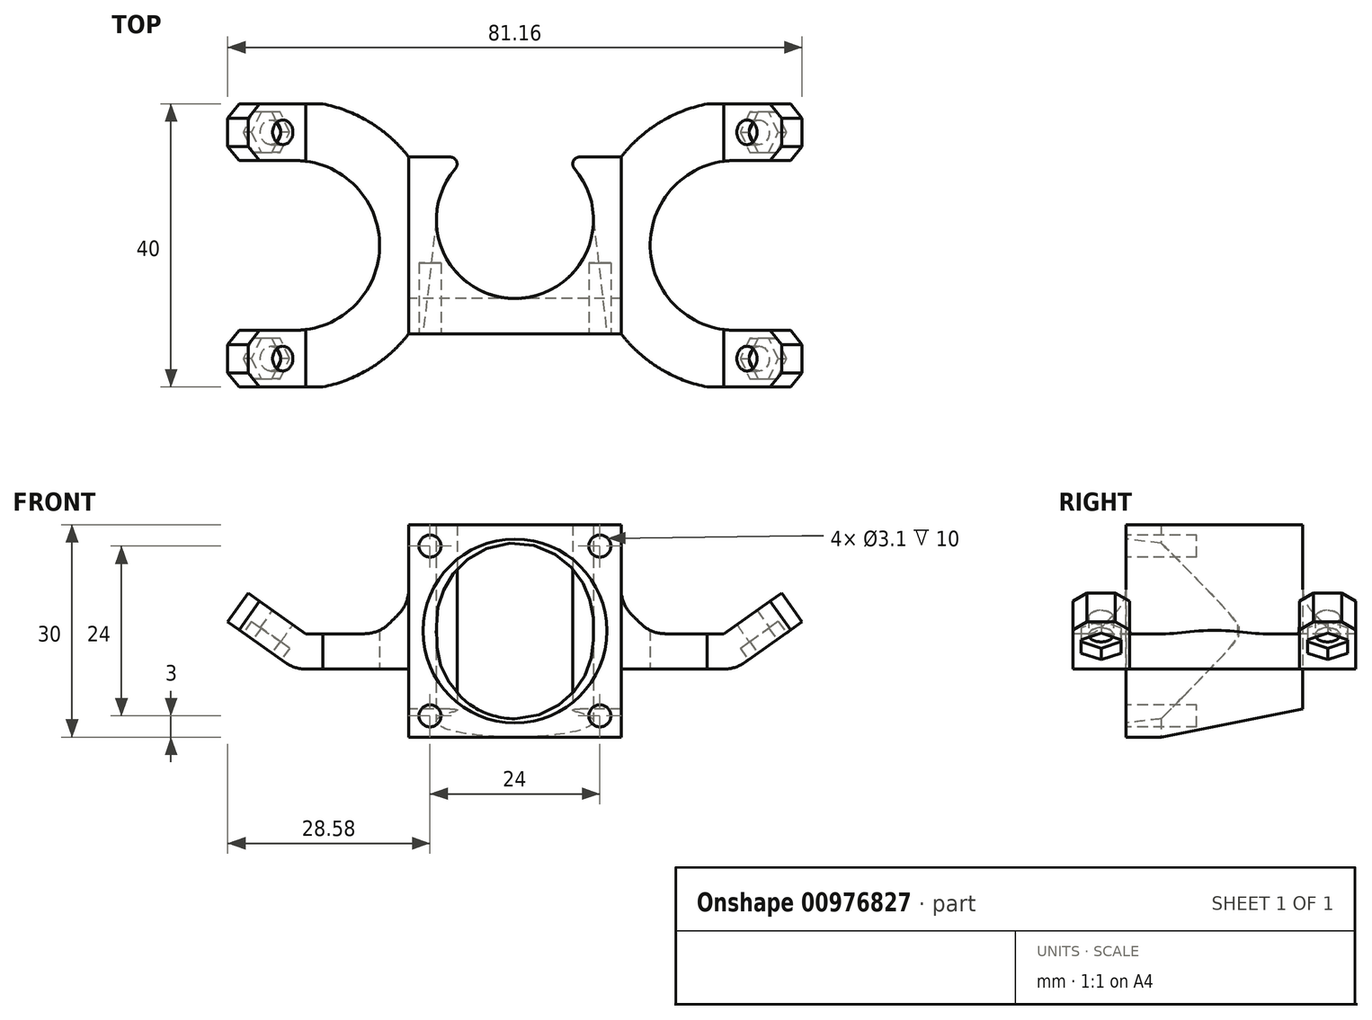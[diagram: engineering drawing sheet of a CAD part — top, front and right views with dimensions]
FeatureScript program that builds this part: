
annotation { "Feature Type Name" : "Feature", "Feature Type Description" : "" }
export const myFeature = defineFeature(function(context is Context, id is Id, definition is map)
    precondition{}
    {
        {
            var Q0;
            Q0=qCreatedBy(makeId("Top.planeOp"),FACE);
            var sketch = newSketch(context, id + "F0", { "sketchPlane" : qUnion([Q0])});
            skLineSegment(sketch, "E0.bottom", {"start": v(0, 0) * mm, "end": v(30, 0) * mm});
            skLineSegment(sketch, "E0.top", {"start": v(0, 25) * mm, "end": v(8.37, 25) * mm});
            skLineSegment(sketch, "E0.left", {"start": v(0, 0) * mm, "end": v(0, 25) * mm});
            skLineSegment(sketch, "E0.right", {"start": v(30, 0) * mm, "end": v(30, 25) * mm});
            skArc(sketch, "E1", {"start": v(8.37, 25) * mm, "mid": v(15, 5) * mm, "end": v(21.63, 25) * mm});
            skPoint(sketch, "E1.centerSnap0", {"position": v(15, 25) * mm});
            skLineSegment(sketch, "E2.trimOffspring", {"start": v(21.63, 25) * mm, "end": v(30, 25) * mm});
            skSolve(sketch);
        }
        {
            var Q0;
            Q0=qSketchRegion(id+"F0",true);
            extrude(context, id + "F1", {"entities" : qUnion([Q0]), "depth" : 30 * mm});
        }
        {
            var Q0;
            Q0=makeQuery(id+"F1.opExtrude","SWEPT_FACE",FACE,{"disambiguationData":[OSD([sQuery(id+"F0.wireOp",EDGE,"E0.left")])]});
            var sketch = newSketch(context, id + "F2", { "sketchPlane" : qUnion([Q0])});
            skLineSegment(sketch, "E3", {"start": v(-25, 4) * mm, "end": v(-5, 0) * mm});
            skLineSegment(sketch, "E4", {"start": v(-5, 0) * mm, "end": v(-25, 0) * mm});
            skLineSegment(sketch, "E5", {"start": v(-25, 0) * mm, "end": v(-25, 4) * mm});
            skSolve(sketch);
        }
        {
            var Q0;
            Q0=makeQuery(id+"F2.imprint","IMPRINT",FACE,{"disambiguationData":[TD([[makeQuery(id+"F2.imprint","IMPRINT",EDGE,{"derivedFrom":sQuery(id+"F2.wireOp",EDGE,"E3")}),-1.0]])]});
            extrude(context, id + "F3", {"entities" : qUnion([Q0]), "operationType" : NewBodyOperationType.REMOVE, "endBound" : BoundingType.THROUGH_ALL, "oppositeDirection" : true, "depth" : 25 * mm});
        }
        {
            var Q0;
            Q0=makeQuery(id+"F1.opExtrude","CAP_FACE",FACE,{"disambiguationData":[OSD([sQuery(id+"F0.wireOp",EDGE,"E0.bottom"),sQuery(id+"F0.wireOp",EDGE,"E0.top"),sQuery(id+"F0.wireOp",EDGE,"E0.left"),sQuery(id+"F0.wireOp",EDGE,"E0.right"),sQuery(id+"F0.wireOp",EDGE,"E1"),sQuery(id+"F0.wireOp",EDGE,"E2.trimOffspring")])],"isStart":false});
            cPlane(context, id + "F4", {"entities" : qUnion([Q0]), "cplaneType" : CPlaneType.OFFSET, "offset" : 15 * mm, "oppositeDirection" : true, "width" : 150 * mm, "height" : 150 * mm});
        }
        {
            var Q0;
            Q0=qCreatedBy(id+"F4.planeOp",FACE);
            var sketch = newSketch(context, id + "F5", { "sketchPlane" : qUnion([Q0])});
            skArc(sketch, "E6.0.0", {"start": v(15, 5) * mm, "mid": v(7.15, 8.25) * mm, "end": v(3.9, 16.1) * mm});
            skLineSegment(sketch, "E6.0.1", {"start": v(8.37, 25) * mm, "end": v(0, 25) * mm, "construction": true});
            skLineSegment(sketch, "E6.0.2", {"start": v(0, 25) * mm, "end": v(0, 0) * mm, "construction": true});
            skLineSegment(sketch, "E6.0.3", {"start": v(0, 0) * mm, "end": v(30, 0) * mm, "construction": true});
            skLineSegment(sketch, "E6.0.4", {"start": v(30, 0) * mm, "end": v(30, 25) * mm, "construction": true});
            skLineSegment(sketch, "E6.0.5", {"start": v(30, 25) * mm, "end": v(21.63, 25) * mm, "construction": true});
            skLineSegment(sketch, "E7", {"start": v(3.9, 16.1) * mm, "end": v(2, 0) * mm});
            skLineSegment(sketch, "E8", {"start": v(2, 0) * mm, "end": v(15, 0) * mm});
            skLineSegment(sketch, "E9", {"start": v(15, 0) * mm, "end": v(15, 5) * mm});
            skLineSegment(sketch, "E10", {"start": v(15, 16.1) * mm, "end": v(15, 5) * mm, "construction": true});
            skSolve(sketch);
        }
        {
            var Q0;
            Q0=qSketchRegion(id+"F5",true);
            var Q1;
            Q1=sQuery(id+"F5.wireOp",EDGE,"E10");
            revolve(context, id + "F6", {"operationType" : NewBodyOperationType.REMOVE, "entities" : qUnion([Q0]), "axis" : qUnion([Q1]), "revolveType" : RevolveType.FULL, "oppositeDirection" : true});
        }
        {
            var Q0;
            Q0=makeQuery(id+"F1.opExtrude","SWEPT_FACE",FACE,{"disambiguationData":[OSD([sQuery(id+"F0.wireOp",EDGE,"E0.bottom")])]});
            var sketch = newSketch(context, id + "F7", { "sketchPlane" : qUnion([Q0])});
            skCircle(sketch, "E11", {"center": v(3, 27) * mm, "radius": 1.55 * mm});
            skCircle(sketch, "E12", {"center": v(27, 27) * mm, "radius": 1.55 * mm});
            skCircle(sketch, "E13", {"center": v(27, 3) * mm, "radius": 1.55 * mm});
            skCircle(sketch, "E14", {"center": v(3, 3) * mm, "radius": 1.55 * mm});
            skSolve(sketch);
        }
        {
            var Q0;
            Q0=qSketchRegion(id+"F7",true);
            extrude(context, id + "F8", {"entities" : qUnion([Q0]), "operationType" : NewBodyOperationType.REMOVE, "oppositeDirection" : true, "depth" : 10 * mm});
        }
        {
            var Q0;
            Q0=makeQuery(id+"F11.boolean.opBoolean","MERGE",FACE,{"derivedFrom":[makeQuery(id+"F1.opExtrude","SWEPT_FACE",FACE,{"disambiguationData":[OSD([sQuery(id+"F0.wireOp",EDGE,"E0.bottom")])]}),makeQuery(id+"F11.opExtrude","CAP_FACE",FACE,{"disambiguationData":[OSD([sQuery(id+"F10.wireOp",EDGE,"E15"),sQuery(id+"F10.wireOp",EDGE,"2PUToxiN-oQwl-tIPs-fLwY-Sr81A9apaHCL"),sQuery(id+"F10.wireOp",EDGE,"E16"),sQuery(id+"F10.wireOp",EDGE,"zEtzbMIC-mU0K-EOkH-si9V-q6YdlQpnv3ph")])],"isStart":true}),makeQuery(id+"F11.opExtrude","CAP_FACE",FACE,{"disambiguationData":[OSD([sQuery(id+"F10.wireOp",EDGE,"f055ece5-383d-490e-b074-d048fb5212010.MirrorCS"),sQuery(id+"F10.wireOp",EDGE,"f055ece5-383d-490e-b074-d048fb5212011.MirrorCS"),sQuery(id+"F10.wireOp",EDGE,"f055ece5-383d-490e-b074-d048fb5212012.MirrorCS"),sQuery(id+"F10.wireOp",EDGE,"f055ece5-383d-490e-b074-d048fb5212013.MirrorCS")])],"isStart":true})]});
            cPlane(context, id + "F9", {"entities" : qUnion([Q0]), "cplaneType" : CPlaneType.OFFSET, "offset" : 7.5 * mm, "width" : 150 * mm, "height" : 150 * mm});
        }
        {
            var Q0;
            Q0=qCreatedBy(id+"F9.planeOp",FACE);
            var sketch = newSketch(context, id + "F10", { "sketchPlane" : qUnion([Q0])});
            skLineSegment(sketch, "E15", {"start": v(-22.7, 20.37) * mm, "end": v(-14.52, 14.6) * mm});
            skLineSegment(sketch, "E16", {"start": v(-16.1, 9.6) * mm, "end": v(-25.58, 16.28) * mm});
            skLineSegment(sketch, "E17", {"start": v(15, 30) * mm, "end": v(15, 0) * mm, "construction": true});
            skLineSegment(sketch, "E18", {"start": v(15, 30) * mm, "end": v(15, 60) * mm, "construction": true});
            skLineSegment(sketch, "E19", {"start": v(-47.22, 37.65) * mm, "end": v(-35.7, 54) * mm, "construction": true});
            skLineSegment(sketch, "E20.bottom", {"start": v(8, 30) * mm, "end": v(22, 30) * mm, "construction": true});
            skLineSegment(sketch, "E20.top", {"start": v(8, 55) * mm, "end": v(22, 55) * mm, "construction": true});
            skLineSegment(sketch, "E20.left", {"start": v(8, 30) * mm, "end": v(8, 55) * mm, "construction": true});
            skLineSegment(sketch, "E20.right", {"start": v(22, 30) * mm, "end": v(22, 55) * mm, "construction": true});
            skPoint(sketch, "E20.middle", {"position": v(15, 42.5) * mm});
            skLineSegment(sketch, "E21.0.0", {"start": v(0, 0) * mm, "end": v(30, 0) * mm});
            skLineSegment(sketch, "E21.0.1", {"start": v(30, 0) * mm, "end": v(30, 30) * mm});
            skLineSegment(sketch, "E21.0.2", {"start": v(30, 30) * mm, "end": v(0, 30) * mm});
            skLineSegment(sketch, "E22", {"start": v(-35.7, 54) * mm, "end": v(-3, 30.95) * mm, "construction": true});
            skLineSegment(sketch, "E23", {"start": v(-3, 30.95) * mm, "end": v(-14.52, 14.6) * mm, "construction": true});
            skLineSegment(sketch, "E24", {"start": v(-22.7, 20.37) * mm, "end": v(-25.58, 16.28) * mm});
            skLineSegment(sketch, "E25", {"start": v(-14.52, 14.6) * mm, "end": v(0, 14.6) * mm});
            skLineSegment(sketch, "E26", {"start": v(0, 14.6) * mm, "end": v(0, 9.6) * mm});
            skLineSegment(sketch, "E27", {"start": v(0, 9.6) * mm, "end": v(-16.1, 9.6) * mm});
            skLineSegment(sketch, "E28.MirrorCS", {"start": v(46.1, 9.6) * mm, "end": v(55.58, 16.28) * mm});
            skLineSegment(sketch, "E29.MirrorCS", {"start": v(52.7, 20.37) * mm, "end": v(44.52, 14.6) * mm});
            skLineSegment(sketch, "E30.MirrorCS", {"start": v(44.52, 14.6) * mm, "end": v(30, 14.6) * mm});
            skLineSegment(sketch, "E31.MirrorCS", {"start": v(30, 9.6) * mm, "end": v(46.1, 9.6) * mm});
            skLineSegment(sketch, "E32.MirrorCS", {"start": v(52.7, 20.37) * mm, "end": v(55.58, 16.28) * mm});
            skLineSegment(sketch, "E33.MirrorCS", {"start": v(30, 14.6) * mm, "end": v(30, 9.6) * mm});
            skSolve(sketch);
        }
        {
            var Q0;
            Q0 = qSketchRegion(id + "F10", true);
            var Q1;
            Q1=makeQuery(id+"F1.opExtrude","SWEPT_FACE",FACE,{"disambiguationData":[OSD([sQuery(id+"F0.wireOp",EDGE,"E2.trimOffspring")])]});
            extrude(context, id + "F11", {"entities" : qUnion([Q0]), "operationType" : NewBodyOperationType.ADD, "oppositeDirection" : true, "depth" : 40 * mm, "endBoundEntityFace" : qUnion([Q1]), "offsetDistance" : 25 * mm});
        }
        {
            var Q0;
            Q0=makeQuery(id+"F11.opExtrude","SWEPT_FACE",FACE,{"disambiguationData":[OSD([sQuery(id+"F10.wireOp",EDGE,"E27")])]});
            var sketch = newSketch(context, id + "F12", { "sketchPlane" : qUnion([Q0])});
            skLineSegment(sketch, "E34.0.0", {"start": v(-16.1, 7.5) * mm, "end": v(-25.58, 7.5) * mm, "construction": true});
            skLineSegment(sketch, "E34.0.1", {"start": v(-25.58, 7.5) * mm, "end": v(-25.58, -32.5) * mm, "construction": true});
            skLineSegment(sketch, "E34.0.2", {"start": v(-25.58, -32.5) * mm, "end": v(-16.1, -32.5) * mm, "construction": true});
            skLineSegment(sketch, "E34.0.3", {"start": v(-16.1, -32.5) * mm, "end": v(-16.1, 7.5) * mm, "construction": true});
            skLineSegment(sketch, "E35", {"start": v(-25.58, -24.5) * mm, "end": v(-25.58, -0.5) * mm});
            skLineSegment(sketch, "E36", {"start": v(-25.58, -0.5) * mm, "end": v(-16.1, -0.5) * mm});
            skLineSegment(sketch, "E37", {"start": v(-25.58, -24.5) * mm, "end": v(-16.1, -24.5) * mm});
            skArc(sketch, "E38", {"start": v(-16.1, -24.5) * mm, "mid": v(-4.1, -12.5) * mm, "end": v(-16.1, -0.5) * mm});
            skArc(sketch, "E39.0", {"start": v(-16.1, -32.9) * mm, "mid": v(-14.11, -32.8) * mm, "end": v(-12.14, -32.5) * mm, "construction": true});
            skPoint(sketch, "E40", {"position": v(0, 0) * mm});
            skLineSegment(sketch, "E41", {"start": v(-12.14, 7.5) * mm, "end": v(0, 7.5) * mm});
            skLineSegment(sketch, "E42", {"start": v(0, 7.5) * mm, "end": v(0, 0) * mm});
            skLineSegment(sketch, "E43", {"start": v(-12.14, -32.5) * mm, "end": v(0, -32.5) * mm});
            skLineSegment(sketch, "E44", {"start": v(0, -32.5) * mm, "end": v(0, -25) * mm});
            skArc(sketch, "E45", {"start": v(-12.14, 7.5) * mm, "mid": v(-14.11, 7.8) * mm, "end": v(-16.1, 7.9) * mm, "construction": true});
            skArc(sketch, "E46", {"start": v(-12.14, -32.5) * mm, "mid": v(-5.4, -29.85) * mm, "end": v(0, -25) * mm});
            skArc(sketch, "E47", {"start": v(0, 0) * mm, "mid": v(-5.4, 4.85) * mm, "end": v(-12.14, 7.5) * mm});
            skLineSegment(sketch, "E48", {"start": v(0, -25) * mm, "end": v(0, -25) * mm});
            skArc(sketch, "E49", {"start": v(0, -25) * mm, "mid": v(4.28, -12.5) * mm, "end": v(0, 0) * mm, "construction": true});
            skLineSegment(sketch, "E50.0.0", {"start": v(15, -5) * mm, "end": v(30, -5) * mm, "construction": true});
            skLineSegment(sketch, "E50.0.1", {"start": v(30, -5) * mm, "end": v(30, 0) * mm, "construction": true});
            skLineSegment(sketch, "E50.0.2", {"start": v(30, 0) * mm, "end": v(0, 0) * mm, "construction": true});
            skLineSegment(sketch, "E50.0.3", {"start": v(0, 0) * mm, "end": v(0, -5) * mm, "construction": true});
            skLineSegment(sketch, "E50.0.4", {"start": v(0, -5) * mm, "end": v(15, -5) * mm, "construction": true});
            skLineSegment(sketch, "E51", {"start": v(15, -5) * mm, "end": v(15, 0) * mm, "construction": true});
            skArc(sketch, "E52.MirrorCS", {"start": v(42.14, 7.5) * mm, "mid": v(44.11, 7.8) * mm, "end": v(46.1, 7.9) * mm, "construction": true});
            skArc(sketch, "E53.MirrorCS", {"start": v(46.1, -32.9) * mm, "mid": v(44.11, -32.8) * mm, "end": v(42.14, -32.5) * mm, "construction": true});
            skLineSegment(sketch, "E54.MirrorCS", {"start": v(55.58, -24.5) * mm, "end": v(55.58, -0.5) * mm});
            skLineSegment(sketch, "E55.MirrorCS", {"start": v(30, 0) * mm, "end": v(30, -5) * mm});
            skLineSegment(sketch, "E56.MirrorCS", {"start": v(30, -32.5) * mm, "end": v(30, -25) * mm});
            skArc(sketch, "E57.MirrorCS", {"start": v(42.14, -32.5) * mm, "mid": v(35.4, -29.85) * mm, "end": v(30, -25) * mm});
            skLineSegment(sketch, "E58.MirrorCS", {"start": v(55.58, -24.5) * mm, "end": v(46.1, -24.5) * mm});
            skLineSegment(sketch, "E59.MirrorCS", {"start": v(46.1, 7.5) * mm, "end": v(55.58, 7.5) * mm, "construction": true});
            skLineSegment(sketch, "E60.MirrorCS", {"start": v(30, 7.5) * mm, "end": v(30, 0) * mm});
            skLineSegment(sketch, "E61.MirrorCS", {"start": v(42.14, 7.5) * mm, "end": v(30, 7.5) * mm});
            skArc(sketch, "E62.MirrorCS", {"start": v(30, -25) * mm, "mid": v(25.72, -12.5) * mm, "end": v(30, 0) * mm, "construction": true});
            skArc(sketch, "E63.MirrorCS", {"start": v(30, 0) * mm, "mid": v(35.4, 4.85) * mm, "end": v(42.14, 7.5) * mm});
            skLineSegment(sketch, "E64.MirrorCS", {"start": v(55.58, -0.5) * mm, "end": v(46.1, -0.5) * mm});
            skLineSegment(sketch, "E65.MirrorCS", {"start": v(55.58, 7.5) * mm, "end": v(55.58, -32.5) * mm, "construction": true});
            skLineSegment(sketch, "E66.MirrorCS", {"start": v(42.14, -32.5) * mm, "end": v(30, -32.5) * mm});
            skArc(sketch, "E67.MirrorCS", {"start": v(46.1, -24.5) * mm, "mid": v(34.1, -12.5) * mm, "end": v(46.1, -0.5) * mm});
            skPoint(sketch, "E68.MirrorP", {"position": v(30, 0) * mm});
            skLineSegment(sketch, "E69.MirrorCS", {"start": v(30, -25) * mm, "end": v(30, -25) * mm});
            skLineSegment(sketch, "E70.MirrorCS", {"start": v(46.1, -32.5) * mm, "end": v(46.1, 7.5) * mm, "construction": true});
            skLineSegment(sketch, "E71.MirrorCS", {"start": v(55.58, -32.5) * mm, "end": v(46.1, -32.5) * mm, "construction": true});
            skSolve(sketch);
        }
        {
            var Q0;
            Q0 = qSketchRegion(id + "F12", true);
            extrude(context, id + "F13", {"entities" : qUnion([Q0]), "operationType" : NewBodyOperationType.REMOVE, "endBound" : BoundingType.THROUGH_ALL, "oppositeDirection" : true, "depth" : 25 * mm, "offsetDistance" : 25 * mm});
        }
        {
            var Q0;
            Q0=makeQuery(id+"F11.opExtrude","SWEPT_FACE",FACE,{"disambiguationData":[OSD([sQuery(id+"F10.wireOp",EDGE,"E15")])]});
            var sketch = newSketch(context, id + "F14", { "sketchPlane" : qUnion([Q0])});
            skCircle(sketch, "E72", {"center": v(-24.29, -3.5) * mm, "radius": 1.75 * mm});
            skCircle(sketch, "E73", {"center": v(-24.29, 28.5) * mm, "radius": 1.75 * mm});
            skSolve(sketch);
        }
        {
            var Q0;
            Q0 = qSketchRegion(id + "F14", true);
            extrude(context, id + "F15", {"entities" : qUnion([Q0]), "operationType" : NewBodyOperationType.REMOVE, "endBound" : BoundingType.THROUGH_ALL, "oppositeDirection" : true, "depth" : 25 * mm, "offsetDistance" : 25 * mm});
        }
        {
            var Q0;
            {var subQ2=sQuery(id+"F10.wireOp",EDGE,"E16");Q0=makeQuery(id+"F13.boolean.opBoolean","SPLIT",FACE,{"disambiguationData":[TD([makeQuery(id+"F13.opExtrude","SWEPT_FACE",FACE,{"disambiguationData":[OSD([sQuery(id+"F12.wireOp",EDGE,"E36")])]})])],"derivedFrom":makeQuery(id+"F11.opExtrude","SWEPT_FACE",FACE,{"disambiguationData":[OSD([subQ2])]})});}
            var sketch = newSketch(context, id + "F16", { "sketchPlane" : qUnion([Q0])});
            skCircle(sketch, "E74.cCircle", {"center": v(-24.29, 3.5) * mm, "radius": 2.85 * mm, "construction": true});
            skLineSegment(sketch, "E74.0", {"start": v(-22.64, 0.65) * mm, "end": v(-25.93, 0.65) * mm});
            skLineSegment(sketch, "E74.1", {"start": v(-25.93, 0.65) * mm, "end": v(-27.58, 3.5) * mm});
            skLineSegment(sketch, "E74.2", {"start": v(-27.58, 3.5) * mm, "end": v(-25.93, 6.35) * mm});
            skLineSegment(sketch, "E74.3", {"start": v(-25.93, 6.35) * mm, "end": v(-22.64, 6.35) * mm});
            skLineSegment(sketch, "E74.4", {"start": v(-22.64, 6.35) * mm, "end": v(-21, 3.5) * mm});
            skLineSegment(sketch, "E74.5", {"start": v(-21, 3.5) * mm, "end": v(-22.64, 0.65) * mm});
            skPoint(sketch, "E74.0.midPoint", {"position": v(-24.29, 0.65) * mm});
            skCircle(sketch, "E75.0", {"center": v(-24.29, -28.5) * mm, "radius": 1.75 * mm});
            skCircle(sketch, "E76.cCircle", {"center": v(-24.29, -28.5) * mm, "radius": 2.85 * mm});
            skLineSegment(sketch, "E76.0", {"start": v(-22.64, -31.35) * mm, "end": v(-25.93, -31.35) * mm});
            skLineSegment(sketch, "E76.1", {"start": v(-25.93, -31.35) * mm, "end": v(-27.58, -28.5) * mm});
            skLineSegment(sketch, "E76.2", {"start": v(-27.58, -28.5) * mm, "end": v(-25.93, -25.65) * mm});
            skLineSegment(sketch, "E76.3", {"start": v(-25.93, -25.65) * mm, "end": v(-22.64, -25.65) * mm});
            skLineSegment(sketch, "E76.4", {"start": v(-22.64, -25.65) * mm, "end": v(-21, -28.5) * mm});
            skLineSegment(sketch, "E76.5", {"start": v(-21, -28.5) * mm, "end": v(-22.64, -31.35) * mm});
            skPoint(sketch, "E76.0.midPoint", {"position": v(-24.29, -31.35) * mm});
            skSolve(sketch);
        }
        {
            var Q0;
            Q0 = qSketchRegion(id + "F16", true);
            extrude(context, id + "F17", {"entities" : qUnion([Q0]), "operationType" : NewBodyOperationType.REMOVE, "oppositeDirection" : true, "depth" : 2 * mm, "offsetDistance" : 25 * mm});
        }
        {
            var Q0;
            {var subQ2=sQuery(id+"F10.wireOp",EDGE,"E28.MirrorCS");Q0=makeQuery(id+"F13.boolean.opBoolean","SPLIT",FACE,{"disambiguationData":[TD([makeQuery(id+"F13.opExtrude","SWEPT_FACE",FACE,{"disambiguationData":[OSD([sQuery(id+"F12.wireOp",EDGE,"E58.MirrorCS")])]})])],"derivedFrom":makeQuery(id+"F11.opExtrude","SWEPT_FACE",FACE,{"disambiguationData":[OSD([subQ2])]})});}
            var sketch = newSketch(context, id + "F18", { "sketchPlane" : qUnion([Q0])});
            skCircle(sketch, "E77", {"center": v(48.8, -28.5) * mm, "radius": 1.75 * mm});
            skPoint(sketch, "E77.centerSnap0", {"position": v(54.8, -28.5) * mm});
            skLineSegment(sketch, "E78.0.0", {"start": v(43.22, -0.5) * mm, "end": v(54.8, -0.5) * mm, "construction": true});
            skLineSegment(sketch, "E78.0.1", {"start": v(54.8, -0.5) * mm, "end": v(54.8, 7.5) * mm, "construction": true});
            skLineSegment(sketch, "E78.0.2", {"start": v(54.8, 7.5) * mm, "end": v(43.22, 7.5) * mm, "construction": true});
            skLineSegment(sketch, "E78.0.3", {"start": v(43.22, 7.5) * mm, "end": v(43.22, -0.5) * mm, "construction": true});
            skCircle(sketch, "E79", {"center": v(48.8, 3.5) * mm, "radius": 1.75 * mm});
            skPoint(sketch, "E79.centerSnap0", {"position": v(54.8, 3.5) * mm});
            skLineSegment(sketch, "E80.0.0", {"start": v(44.8, -32.5) * mm, "end": v(44.8, -24.4) * mm, "construction": true});
            skEllipticalArc(sketch, "E80.0.1", {"construction": true});
            skLineSegment(sketch, "E80.0.2", {"start": v(46.75, -24.5) * mm, "end": v(54.8, -24.5) * mm, "construction": true});
            skLineSegment(sketch, "E80.0.3", {"start": v(54.8, -24.5) * mm, "end": v(54.8, -32.5) * mm, "construction": true});
            skLineSegment(sketch, "E80.0.4", {"start": v(54.8, -32.5) * mm, "end": v(44.8, -32.5) * mm, "construction": true});
            const initialGuessF18  = {"E80.0.1": [0.046745217764877306, -0.0125, -1, 0, 0.014682579421778443, 0.012, 1.4382942469065467, 1.5707963267948966]};
            skSetInitialGuess(sketch, initialGuessF18);
            skSolve(sketch);
        }
        {
            var Q0;
            Q0 = qSketchRegion(id + "F18", true);
            extrude(context, id + "F19", {"entities" : qUnion([Q0]), "operationType" : NewBodyOperationType.REMOVE, "endBound" : BoundingType.THROUGH_ALL, "oppositeDirection" : true, "depth" : 25 * mm, "offsetDistance" : 25 * mm});
        }
        {
            var Q0;
            {var subQ2=sQuery(id+"F10.wireOp",EDGE,"E28.MirrorCS");Q0=makeQuery(id+"F13.boolean.opBoolean","SPLIT",FACE,{"disambiguationData":[TD([makeQuery(id+"F13.opExtrude","SWEPT_FACE",FACE,{"disambiguationData":[OSD([sQuery(id+"F12.wireOp",EDGE,"E58.MirrorCS")])]})])],"derivedFrom":makeQuery(id+"F11.opExtrude","SWEPT_FACE",FACE,{"disambiguationData":[OSD([subQ2])]})});}
            var sketch = newSketch(context, id + "F20", { "sketchPlane" : qUnion([Q0])});
            skCircle(sketch, "E81.cCircle", {"center": v(48.8, -28.5) * mm, "radius": 2.85 * mm, "construction": true});
            skLineSegment(sketch, "E81.0", {"start": v(47.16, -25.65) * mm, "end": v(50.45, -25.65) * mm});
            skLineSegment(sketch, "E81.1", {"start": v(50.45, -25.65) * mm, "end": v(52.1, -28.5) * mm});
            skLineSegment(sketch, "E81.2", {"start": v(52.1, -28.5) * mm, "end": v(50.45, -31.35) * mm});
            skLineSegment(sketch, "E81.3", {"start": v(50.45, -31.35) * mm, "end": v(47.16, -31.35) * mm});
            skLineSegment(sketch, "E81.4", {"start": v(47.16, -31.35) * mm, "end": v(45.51, -28.5) * mm});
            skLineSegment(sketch, "E81.5", {"start": v(45.51, -28.5) * mm, "end": v(47.16, -25.65) * mm});
            skPoint(sketch, "E81.0.midPoint", {"position": v(48.8, -25.65) * mm});
            skLineSegment(sketch, "E82.0.0", {"start": v(43.22, -0.5) * mm, "end": v(54.8, -0.5) * mm, "construction": true});
            skLineSegment(sketch, "E82.0.1", {"start": v(54.8, -0.5) * mm, "end": v(54.8, 7.5) * mm, "construction": true});
            skLineSegment(sketch, "E82.0.2", {"start": v(54.8, 7.5) * mm, "end": v(43.22, 7.5) * mm, "construction": true});
            skLineSegment(sketch, "E82.0.3", {"start": v(43.22, 7.5) * mm, "end": v(43.22, -0.5) * mm, "construction": true});
            skCircle(sketch, "E83.0", {"center": v(48.8, 3.5) * mm, "radius": 1.75 * mm, "construction": true});
            skCircle(sketch, "E84.cCircle", {"center": v(48.8, 3.5) * mm, "radius": 2.85 * mm, "construction": true});
            skLineSegment(sketch, "E84.0", {"start": v(47.16, 6.35) * mm, "end": v(50.45, 6.35) * mm});
            skLineSegment(sketch, "E84.1", {"start": v(50.45, 6.35) * mm, "end": v(52.1, 3.5) * mm});
            skLineSegment(sketch, "E84.2", {"start": v(52.1, 3.5) * mm, "end": v(50.45, 0.65) * mm});
            skLineSegment(sketch, "E84.3", {"start": v(50.45, 0.65) * mm, "end": v(47.16, 0.65) * mm});
            skLineSegment(sketch, "E84.4", {"start": v(47.16, 0.65) * mm, "end": v(45.51, 3.5) * mm});
            skLineSegment(sketch, "E84.5", {"start": v(45.51, 3.5) * mm, "end": v(47.16, 6.35) * mm});
            skPoint(sketch, "E84.0.midPoint", {"position": v(48.8, 6.35) * mm});
            skSolve(sketch);
        }
        {
            var Q0;
            Q0 = qSketchRegion(id + "F20", true);
            extrude(context, id + "F21", {"entities" : qUnion([Q0]), "operationType" : NewBodyOperationType.REMOVE, "oppositeDirection" : true, "depth" : 2 * mm, "offsetDistance" : 25 * mm});
        }
        {
            var Q0;
            Q0=makeQuery(id+"F11.opExtrude","CAP_EDGE",EDGE,{"disambiguationData":[OSD([sQuery(id+"F10.wireOp",EDGE,"E32.MirrorCS")])],"isStart":false});
            var Q1;
            Q1=makeQuery(id+"F13.boolean.opBoolean","INTERSECT",EDGE,{"derivedFrom":[makeQuery(id+"F11.opExtrude","SWEPT_FACE",FACE,{"disambiguationData":[OSD([sQuery(id+"F10.wireOp",EDGE,"E32.MirrorCS")])]}),makeQuery(id+"F13.opExtrude","SWEPT_FACE",FACE,{"disambiguationData":[OSD([sQuery(id+"F12.wireOp",EDGE,"E58.MirrorCS")])]})]});
            var Q2;
            Q2=makeQuery(id+"F13.boolean.opBoolean","INTERSECT",EDGE,{"derivedFrom":[makeQuery(id+"F11.opExtrude","SWEPT_FACE",FACE,{"disambiguationData":[OSD([sQuery(id+"F10.wireOp",EDGE,"E32.MirrorCS")])]}),makeQuery(id+"F13.opExtrude","SWEPT_FACE",FACE,{"disambiguationData":[OSD([sQuery(id+"F12.wireOp",EDGE,"E64.MirrorCS")])]})]});
            var Q3;
            Q3=makeQuery(id+"F11.opExtrude","CAP_EDGE",EDGE,{"disambiguationData":[OSD([sQuery(id+"F10.wireOp",EDGE,"E32.MirrorCS")])],"isStart":true});
            var Q4;
            Q4=makeQuery(id+"F11.opExtrude","CAP_EDGE",EDGE,{"disambiguationData":[OSD([sQuery(id+"F10.wireOp",EDGE,"E24")])],"isStart":true});
            var Q5;
            Q5=makeQuery(id+"F13.boolean.opBoolean","INTERSECT",EDGE,{"derivedFrom":[makeQuery(id+"F11.opExtrude","SWEPT_FACE",FACE,{"disambiguationData":[OSD([sQuery(id+"F10.wireOp",EDGE,"E24")])]}),makeQuery(id+"F13.opExtrude","SWEPT_FACE",FACE,{"disambiguationData":[OSD([sQuery(id+"F12.wireOp",EDGE,"E36")])]})]});
            var Q6;
            Q6=makeQuery(id+"F13.boolean.opBoolean","INTERSECT",EDGE,{"derivedFrom":[makeQuery(id+"F11.opExtrude","SWEPT_FACE",FACE,{"disambiguationData":[OSD([sQuery(id+"F10.wireOp",EDGE,"E24")])]}),makeQuery(id+"F13.opExtrude","SWEPT_FACE",FACE,{"disambiguationData":[OSD([sQuery(id+"F12.wireOp",EDGE,"E37")])]})]});
            var Q7;
            Q7=makeQuery(id+"F11.opExtrude","CAP_EDGE",EDGE,{"disambiguationData":[OSD([sQuery(id+"F10.wireOp",EDGE,"E24")])],"isStart":false});
            chamfer(context, id + "F22", {"entities" : qUnion([Q0, Q1, Q2, Q3, Q4, Q5, Q6, Q7]), "width" : 2 * mm, "tangentPropagation" : true});
        }
        {
            var Q0;
            Q0=makeQuery(id+"F1.opExtrude","SWEPT_EDGE",EDGE,{"disambiguationData":[OSD([sQuery(id+"F0.wireOp",EDGE,"E0.top"),sQuery(id+"F0.wireOp",EDGE,"E1")])]});
            var Q1;
            Q1=makeQuery(id+"F1.opExtrude","SWEPT_EDGE",EDGE,{"disambiguationData":[OSD([sQuery(id+"F0.wireOp",EDGE,"E1"),sQuery(id+"F0.wireOp",EDGE,"E2.trimOffspring")])]});
            fillet(context, id + "F23", {"entities" : qUnion([Q0, Q1]), "radius" : 1 * mm, "tangentPropagation" : true, "allowEdgeOverflow" : false});
        }
        {
            var Q0;
            {var subQ0=sQuery(id+"F10.wireOp",EDGE,"E25");Q0=makeQuery(id+"F11.boolean.opBoolean","SPLIT",EDGE,{"disambiguationData":[topologyDisambiguationEdgeConnected([makeQuery(id+"F1.opExtrude","SWEPT_FACE",FACE,{"disambiguationData":[OSD([sQuery(id+"F0.wireOp",EDGE,"E0.left")])]}),makeQuery(id+"F11.opExtrude","SWEPT_FACE",FACE,{"disambiguationData":[OSD([subQ0])]})])],"derivedFrom":makeQuery(id+"F11.opExtrude","SWEPT_EDGE",EDGE,{"disambiguationData":[OSD([subQ0,sQuery(id+"F10.wireOp",EDGE,"E26")])]})});}
            var Q1;
            {var subQ0=sQuery(id+"F10.wireOp",EDGE,"E30.MirrorCS");Q1=makeQuery(id+"F11.boolean.opBoolean","SPLIT",EDGE,{"disambiguationData":[topologyDisambiguationEdgeConnected([makeQuery(id+"F1.opExtrude","SWEPT_FACE",FACE,{"disambiguationData":[OSD([sQuery(id+"F0.wireOp",EDGE,"E0.right")])]}),makeQuery(id+"F11.opExtrude","SWEPT_FACE",FACE,{"disambiguationData":[OSD([subQ0])]})])],"derivedFrom":makeQuery(id+"F11.opExtrude","SWEPT_EDGE",EDGE,{"disambiguationData":[OSD([subQ0,sQuery(id+"F10.wireOp",EDGE,"E33.MirrorCS")])]})});}
            var Q2;
            {var subQ0=sQuery(id+"F10.wireOp",EDGE,"E27");Q2=makeQuery(id+"F11.boolean.opBoolean","SPLIT",EDGE,{"disambiguationData":[topologyDisambiguationEdgeConnected([makeQuery(id+"F1.opExtrude","SWEPT_FACE",FACE,{"disambiguationData":[OSD([sQuery(id+"F0.wireOp",EDGE,"E0.left")])]}),makeQuery(id+"F11.opExtrude","SWEPT_FACE",FACE,{"disambiguationData":[OSD([subQ0])]})])],"derivedFrom":makeQuery(id+"F11.opExtrude","SWEPT_EDGE",EDGE,{"disambiguationData":[OSD([sQuery(id+"F10.wireOp",EDGE,"E26"),subQ0])]})});}
            var Q3;
            {var subQ0=sQuery(id+"F10.wireOp",EDGE,"E31.MirrorCS");Q3=makeQuery(id+"F11.boolean.opBoolean","SPLIT",EDGE,{"disambiguationData":[topologyDisambiguationEdgeConnected([makeQuery(id+"F1.opExtrude","SWEPT_FACE",FACE,{"disambiguationData":[OSD([sQuery(id+"F0.wireOp",EDGE,"E0.right")])]}),makeQuery(id+"F11.opExtrude","SWEPT_FACE",FACE,{"disambiguationData":[OSD([subQ0])]})])],"derivedFrom":makeQuery(id+"F11.opExtrude","SWEPT_EDGE",EDGE,{"disambiguationData":[OSD([subQ0,sQuery(id+"F10.wireOp",EDGE,"E33.MirrorCS")])]})});}
            chamfer(context, id + "F24", {"entities" : qUnion([Q0, Q1, Q2, Q3]), "width" : 4.2 * mm, "tangentPropagation" : true});
        }
        {
            var Q0;
            {var subQ0=sQuery(id+"F10.wireOp",EDGE,"E25");var subQ1=makeQuery(id+"F11.opExtrude","SWEPT_FACE",FACE,{"disambiguationData":[OSD([subQ0])]});Q0=makeQuery(id+"F24.opChamfer","BLEND_EDGE",EDGE,{"disambiguationData":[OD(1.0)],"blendedFrom":[makeQuery(id+"F11.boolean.opBoolean","SPLIT",EDGE,{"disambiguationData":[topologyDisambiguationEdgeConnected([makeQuery(id+"F1.opExtrude","SWEPT_FACE",FACE,{"disambiguationData":[OSD([sQuery(id+"F0.wireOp",EDGE,"E0.left")])]}),subQ1])],"derivedFrom":makeQuery(id+"F11.opExtrude","SWEPT_EDGE",EDGE,{"disambiguationData":[OSD([subQ0,sQuery(id+"F10.wireOp",EDGE,"E26")])]})}),subQ1],"blendedInto":[subQ1]});}
            var Q1;
            {var subQ0=sQuery(id+"F10.wireOp",EDGE,"E27");var subQ1=makeQuery(id+"F11.opExtrude","SWEPT_FACE",FACE,{"disambiguationData":[OSD([subQ0])]});Q1=makeQuery(id+"F24.opChamfer","BLEND_EDGE",EDGE,{"disambiguationData":[OD(0.0)],"blendedFrom":[makeQuery(id+"F11.boolean.opBoolean","SPLIT",EDGE,{"disambiguationData":[topologyDisambiguationEdgeConnected([makeQuery(id+"F1.opExtrude","SWEPT_FACE",FACE,{"disambiguationData":[OSD([sQuery(id+"F0.wireOp",EDGE,"E0.left")])]}),subQ1])],"derivedFrom":makeQuery(id+"F11.opExtrude","SWEPT_EDGE",EDGE,{"disambiguationData":[OSD([sQuery(id+"F10.wireOp",EDGE,"E26"),subQ0])]})}),subQ1],"blendedInto":[subQ1]});}
            var Q2;
            {var subQ3=sQuery(id+"F0.wireOp",EDGE,"E0.left");var subQ6=makeQuery(id+"F1.opExtrude","SWEPT_FACE",FACE,{"disambiguationData":[OSD([subQ3])]});var subQ8=sQuery(id+"F10.wireOp",EDGE,"E26");var subQ9=sQuery(id+"F10.wireOp",EDGE,"E27");var subQ10=makeQuery(id+"F11.opExtrude","SWEPT_FACE",FACE,{"disambiguationData":[OSD([subQ9])]});Q2=makeQuery(id+"F24.opChamfer","BLEND_EDGE",EDGE,{"blendedFrom":[makeQuery(id+"F11.boolean.opBoolean","SPLIT",EDGE,{"disambiguationData":[topologyDisambiguationEdgeConnected([subQ6,subQ10])],"derivedFrom":makeQuery(id+"F11.opExtrude","SWEPT_EDGE",EDGE,{"disambiguationData":[OSD([subQ8,subQ9])]})}),makeQuery(id+"F11.boolean.opBoolean","SPLIT",FACE,{"disambiguationData":[TD([subQ10])],"derivedFrom":subQ6})],"blendedInto":[makeQuery(id+"F11.boolean.opBoolean","SPLIT",FACE,{"disambiguationData":[TD([subQ10])],"derivedFrom":subQ6})]});}
            var Q3;
            {var subQ1=sQuery(id+"F10.wireOp",EDGE,"E25");var subQ2=makeQuery(id+"F11.opExtrude","SWEPT_FACE",FACE,{"disambiguationData":[OSD([subQ1])]});var subQ3=sQuery(id+"F0.wireOp",EDGE,"E0.left");var subQ5=sQuery(id+"F10.wireOp",EDGE,"E26");var subQ6=makeQuery(id+"F1.opExtrude","SWEPT_FACE",FACE,{"disambiguationData":[OSD([subQ3])]});Q3=makeQuery(id+"F24.opChamfer","BLEND_EDGE",EDGE,{"blendedFrom":[makeQuery(id+"F11.boolean.opBoolean","SPLIT",EDGE,{"disambiguationData":[topologyDisambiguationEdgeConnected([subQ6,subQ2])],"derivedFrom":makeQuery(id+"F11.opExtrude","SWEPT_EDGE",EDGE,{"disambiguationData":[OSD([subQ1,subQ5])]})}),makeQuery(id+"F11.boolean.opBoolean","SPLIT",FACE,{"disambiguationData":[TD([subQ2])],"derivedFrom":subQ6})],"blendedInto":[makeQuery(id+"F11.boolean.opBoolean","SPLIT",FACE,{"disambiguationData":[TD([subQ2])],"derivedFrom":subQ6})]});}
            var Q4;
            {var subQ0=sQuery(id+"F10.wireOp",EDGE,"E30.MirrorCS");var subQ1=makeQuery(id+"F11.opExtrude","SWEPT_FACE",FACE,{"disambiguationData":[OSD([subQ0])]});var subQ3=sQuery(id+"F0.wireOp",EDGE,"E0.right");var subQ5=sQuery(id+"F10.wireOp",EDGE,"E33.MirrorCS");var subQ6=makeQuery(id+"F1.opExtrude","SWEPT_FACE",FACE,{"disambiguationData":[OSD([subQ3])]});Q4=makeQuery(id+"F24.opChamfer","BLEND_EDGE",EDGE,{"blendedFrom":[makeQuery(id+"F11.boolean.opBoolean","SPLIT",EDGE,{"disambiguationData":[topologyDisambiguationEdgeConnected([subQ6,subQ1])],"derivedFrom":makeQuery(id+"F11.opExtrude","SWEPT_EDGE",EDGE,{"disambiguationData":[OSD([subQ0,subQ5])]})}),makeQuery(id+"F11.boolean.opBoolean","SPLIT",FACE,{"disambiguationData":[TD([subQ1])],"derivedFrom":subQ6})],"blendedInto":[makeQuery(id+"F11.boolean.opBoolean","SPLIT",FACE,{"disambiguationData":[TD([subQ1])],"derivedFrom":subQ6})]});}
            var Q5;
            {var subQ0=sQuery(id+"F10.wireOp",EDGE,"E30.MirrorCS");var subQ1=makeQuery(id+"F11.opExtrude","SWEPT_FACE",FACE,{"disambiguationData":[OSD([subQ0])]});Q5=makeQuery(id+"F24.opChamfer","BLEND_EDGE",EDGE,{"disambiguationData":[OD(1.0)],"blendedFrom":[makeQuery(id+"F11.boolean.opBoolean","SPLIT",EDGE,{"disambiguationData":[topologyDisambiguationEdgeConnected([makeQuery(id+"F1.opExtrude","SWEPT_FACE",FACE,{"disambiguationData":[OSD([sQuery(id+"F0.wireOp",EDGE,"E0.right")])]}),subQ1])],"derivedFrom":makeQuery(id+"F11.opExtrude","SWEPT_EDGE",EDGE,{"disambiguationData":[OSD([subQ0,sQuery(id+"F10.wireOp",EDGE,"E33.MirrorCS")])]})}),subQ1],"blendedInto":[subQ1]});}
            var Q6;
            {var subQ0=sQuery(id+"F10.wireOp",EDGE,"E31.MirrorCS");var subQ1=makeQuery(id+"F11.opExtrude","SWEPT_FACE",FACE,{"disambiguationData":[OSD([subQ0])]});Q6=makeQuery(id+"F24.opChamfer","BLEND_EDGE",EDGE,{"disambiguationData":[OD(1.0)],"blendedFrom":[makeQuery(id+"F11.boolean.opBoolean","SPLIT",EDGE,{"disambiguationData":[topologyDisambiguationEdgeConnected([makeQuery(id+"F1.opExtrude","SWEPT_FACE",FACE,{"disambiguationData":[OSD([sQuery(id+"F0.wireOp",EDGE,"E0.right")])]}),subQ1])],"derivedFrom":makeQuery(id+"F11.opExtrude","SWEPT_EDGE",EDGE,{"disambiguationData":[OSD([subQ0,sQuery(id+"F10.wireOp",EDGE,"E33.MirrorCS")])]})}),subQ1],"blendedInto":[subQ1]});}
            var Q7;
            {var subQ2=sQuery(id+"F0.wireOp",EDGE,"E0.right");var subQ3=makeQuery(id+"F1.opExtrude","SWEPT_FACE",FACE,{"disambiguationData":[OSD([subQ2])]});var subQ8=sQuery(id+"F10.wireOp",EDGE,"E31.MirrorCS");var subQ9=makeQuery(id+"F11.opExtrude","SWEPT_FACE",FACE,{"disambiguationData":[OSD([subQ8])]});var subQ10=sQuery(id+"F10.wireOp",EDGE,"E33.MirrorCS");Q7=makeQuery(id+"F24.opChamfer","BLEND_EDGE",EDGE,{"blendedFrom":[makeQuery(id+"F11.boolean.opBoolean","SPLIT",EDGE,{"disambiguationData":[topologyDisambiguationEdgeConnected([subQ3,subQ9])],"derivedFrom":makeQuery(id+"F11.opExtrude","SWEPT_EDGE",EDGE,{"disambiguationData":[OSD([subQ8,subQ10])]})}),makeQuery(id+"F11.boolean.opBoolean","SPLIT",FACE,{"disambiguationData":[TD([subQ9])],"derivedFrom":subQ3})],"blendedInto":[makeQuery(id+"F11.boolean.opBoolean","SPLIT",FACE,{"disambiguationData":[TD([subQ9])],"derivedFrom":subQ3})]});}
            var Q8;
            {var subQ0=sQuery(id+"F10.wireOp",EDGE,"E31.MirrorCS");var subQ1=sQuery(id+"F10.wireOp",EDGE,"E28.MirrorCS");Q8=makeQuery(id+"F13.boolean.opBoolean","SPLIT",EDGE,{"disambiguationData":[TD([makeQuery(id+"F13.opExtrude","SWEPT_FACE",FACE,{"disambiguationData":[OSD([sQuery(id+"F12.wireOp",EDGE,"E64.MirrorCS")])]})])],"derivedFrom":makeQuery(id+"F11.opExtrude","SWEPT_EDGE",EDGE,{"disambiguationData":[OSD([subQ1,subQ0])]})});}
            var Q9;
            {var subQ0=sQuery(id+"F10.wireOp",EDGE,"E31.MirrorCS");var subQ1=sQuery(id+"F10.wireOp",EDGE,"E28.MirrorCS");Q9=makeQuery(id+"F13.boolean.opBoolean","SPLIT",EDGE,{"disambiguationData":[TD([makeQuery(id+"F13.opExtrude","SWEPT_FACE",FACE,{"disambiguationData":[OSD([sQuery(id+"F12.wireOp",EDGE,"E58.MirrorCS")])]})])],"derivedFrom":makeQuery(id+"F11.opExtrude","SWEPT_EDGE",EDGE,{"disambiguationData":[OSD([subQ1,subQ0])]})});}
            var Q10;
            {var subQ0=sQuery(id+"F10.wireOp",EDGE,"E16");var subQ1=sQuery(id+"F10.wireOp",EDGE,"E27");Q10=makeQuery(id+"F13.boolean.opBoolean","SPLIT",EDGE,{"disambiguationData":[TD([makeQuery(id+"F13.opExtrude","SWEPT_FACE",FACE,{"disambiguationData":[OSD([sQuery(id+"F12.wireOp",EDGE,"E37")])]})])],"derivedFrom":makeQuery(id+"F11.opExtrude","SWEPT_EDGE",EDGE,{"disambiguationData":[OSD([subQ0,subQ1])]})});}
            var Q11;
            {var subQ0=sQuery(id+"F10.wireOp",EDGE,"E27");var subQ1=sQuery(id+"F10.wireOp",EDGE,"E16");Q11=makeQuery(id+"F13.boolean.opBoolean","SPLIT",EDGE,{"disambiguationData":[TD([makeQuery(id+"F13.opExtrude","SWEPT_FACE",FACE,{"disambiguationData":[OSD([sQuery(id+"F12.wireOp",EDGE,"E36")])]})])],"derivedFrom":makeQuery(id+"F11.opExtrude","SWEPT_EDGE",EDGE,{"disambiguationData":[OSD([subQ1,subQ0])]})});}
            fillet(context, id + "F25", {"entities" : qUnion([Q0, Q1, Q2, Q3, Q4, Q5, Q6, Q7, Q8, Q9, Q10, Q11]), "radius" : 5 * mm, "tangentPropagation" : true, "allowEdgeOverflow" : false});
        }
    });
